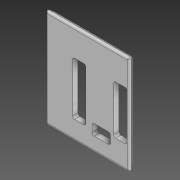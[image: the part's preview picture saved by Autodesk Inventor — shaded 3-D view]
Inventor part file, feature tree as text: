
AUTODESK INVENTOR PART (.ipt)
format: ipt  version: 2021 (Build 250183000, 183)  size: 189,952 bytes
history: native  units: mm
features: extrude x4, sketch x3, fillet x2, other x1
ambient origin geometry x8: Origin, YZ Plane, XZ Plane, XY Plane, X Axis, Y Axis, Z Axis, Center Point
bodies: Body1 (feature_tree)
feature tree (10):
  other  "Sólido1"
  sketch  "Boceto1"  dims[d0=0.35mm d1=5.0mm d2=0.0mm]
  extrude  "Extrusión1"  Depth=5.0mm TaperAngle=0.0deg
  extrude  "Extrusión2"  Depth=6.204268mm
  extrude  "Extrusión3"  Depth=5.0mm TaperAngle=0.0deg
  extrude  "Extrusión4"  Depth=2.0mm
  fillet  "Empalme1"  Radius=2.0mm
  fillet  "Empalme2"  [1 undecoded]
  sketch  "Boceto2"  dims[d3=2.5mm d4=0.0mm]
  sketch  "Boceto3"  dims[d5=4.0mm d6=4.0mm d7=25.797705mm d8=0.67995mm d9=26.985048mm d10=3.061369mm d11=3.544451mm d12=5.0mm d13=0.0mm d14=6.204268mm d15=3.128976mm d16=10.407423mm d17=5.0mm d18=0.0mm d19=2.0mm d20=2.0mm]
note: 1 required parameter value undecoded (feature->parameter linkage not recoverable at this tier; creation-order binding heuristic only, values carry confidence <= 0.55)
